# Revit family: 0047451 Feilo Sylvania Lighting Fixtures START PANEL LED G3 600 NW
name_source: partatom
category: Lighting Fixtures
revit_build: Autodesk Revit 2017 (Build: 20190507_1515(x64)
units: mm (PartAtom-declared; Revit-internal decimal feet)

## family parameters
Cut with Voids When Loaded = Yes
Host = Face
Light Source = Yes
OmniClass Number = 23.80.70.00
OmniClass Title = Lighting
Part Type = Normal
Room Calculation Point = No
Round Connector Dimension = Use Diameter
Shared = No

## types (1)
- 0047451 START PANEL LED G3 600 NW
    Apparent Load = 36 VA
    Assembly Code = D5020200
    AssetType = Fixed
    Color Filter = 16777215
    Cost = 0 $
    Default Elevation = 1219 mm
    Description = LED recessed IP44 panel - 600x600mm in 4000K Neutral White. 4000lm delivered from 36W. 111lm/W total system effciency. Energy efficient driver included as standard. Even distribution of light throughout fixture. Long lifetime of 50,000 hours (L70).
    Dimming Lamp Color Temperature Shift = <None>
    DimmingControlOptions = Non dimmable
    DocumentationLiterature = http://www.sylvania-lighting.com
    DurationUnit = hours
    ElectricShockClassification = Class II
    Emit Shape Visible in Rendering = No
    Emit from Rectangle Length = 556 mm  [stored 1.82415 ft]
    Emit from Rectangle Width = 556 mm  [stored 1.82415 ft]
    ExpectedLife = 50000
    IfcExportAs = IfcLightFixtureType
    IfcExportType = IfcLightFixtureType
    ImpactProtectionIndex = IK02
    IngressProtection = IP44
    InputVoltage = 220-240V~
    Keynote = 16500
    Lamp = LED
    LampColourRenderingIndex = 0
    LampColourTemperature = 4000 K
    LampNominalLuminous = 4000 lm
    LampsType = LED
    LightOutputRatio = 100
    LuminousEfficacy = 111 lm/W
    Manufacturer = Feilo Sylvania
    ManufacturerName = Feilo Sylvania
    Material = powder coated steel + aluminium housing, polycarbonate diffuser
    Model = START PANEL LED G3 600 NW
    ModelNumber = 0047451
    ModelReference = START PANEL LED G3 600 NW
    Name = START PANEL LED G3 600 NW
    NominalDepth = 596 mm  [stored 1.95538 ft]
    NominalHeight = 65 mm  [stored 0.213255 ft]
    NominalLength = 596 mm  [stored 1.95538 ft]
    Photometric Web File = 0047451.ies
    PowerConsumption = 36 W
    PowerFactor = 0
    Tilt Angle = -90.00°
    Type Image = <None>
    TypeName = START PANEL LED G3 600 NW
    URL = http://www.sylvania-lighting.com
    Voltage = 230 V
    Weight = 2.6 kg

note: [stored X ft] marks values corroborated as IEEE doubles in the binary element streams (Revit-internal decimal feet)

## geometry (parser evidence)
native form markers: Sweep x2
no freeform markers — native parametric forms only
